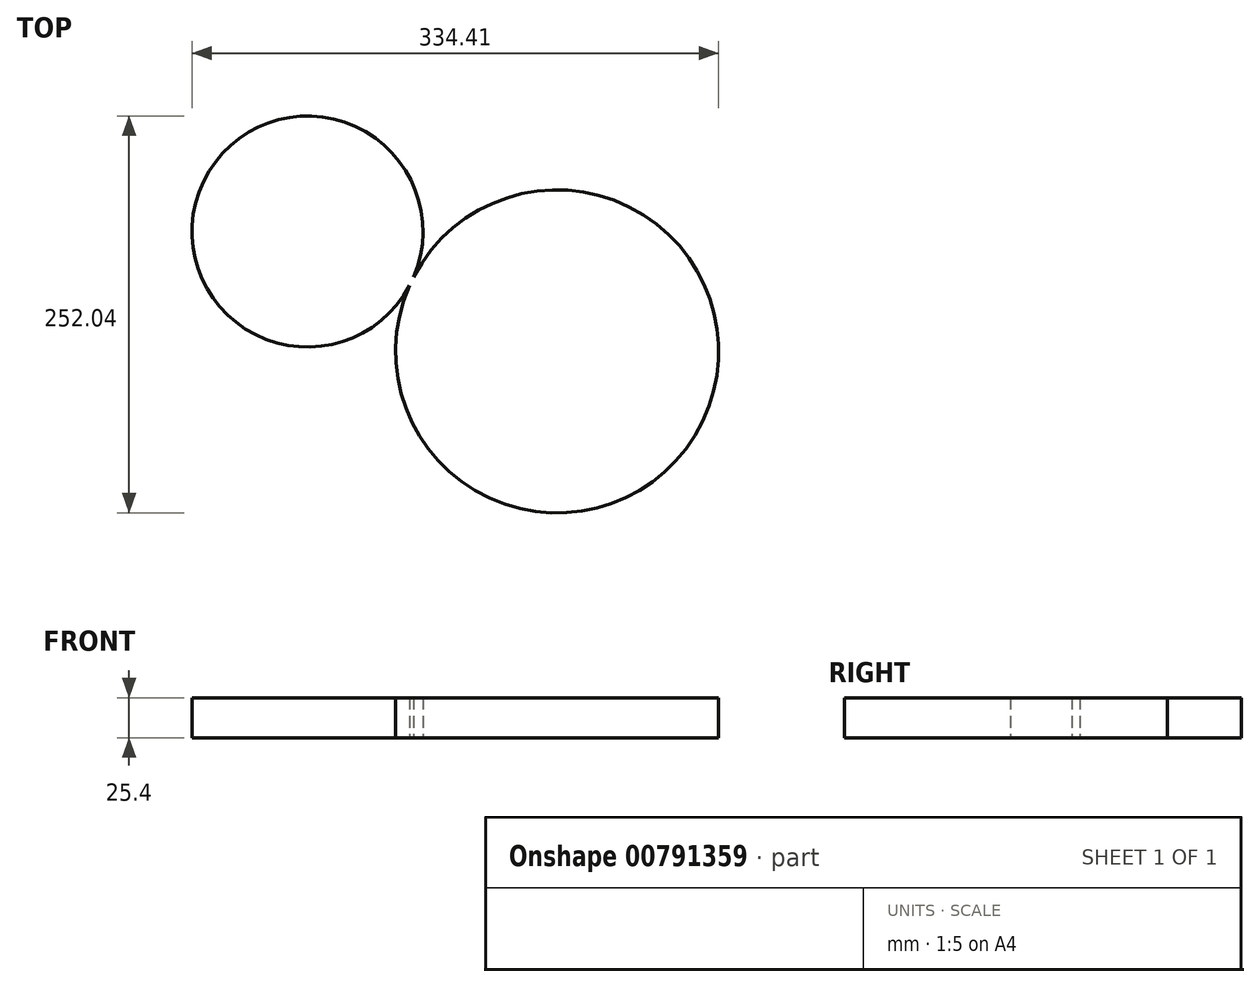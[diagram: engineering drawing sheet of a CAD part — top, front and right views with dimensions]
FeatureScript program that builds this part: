
annotation { "Feature Type Name" : "Feature", "Feature Type Description" : "" }
export const myFeature = defineFeature(function(context is Context, id is Id, definition is map)
    precondition{}
    {
        {
            var Q0;
            Q0=qCreatedBy(makeId("Top.planeOp"),FACE);
            var sketch = newSketch(context, id + "F0", { "sketchPlane" : qUnion([Q0])});
            skCircle(sketch, "E0", {"center": v(-79.18, 20.94) * mm, "radius": 73.35 * mm});
            skCircle(sketch, "E1", {"center": v(79.3, -55.18) * mm, "radius": 102.57 * mm});
            skSolve(sketch);
        }
        {
            var Q0;
            Q0 = qSketchRegion(id + "F0", true);
            extrude(context, id + "F1", {"entities" : qUnion([Q0]), "depth" : 25.4 * mm, "offsetDistance" : 25.4 * mm});
        }
    });
